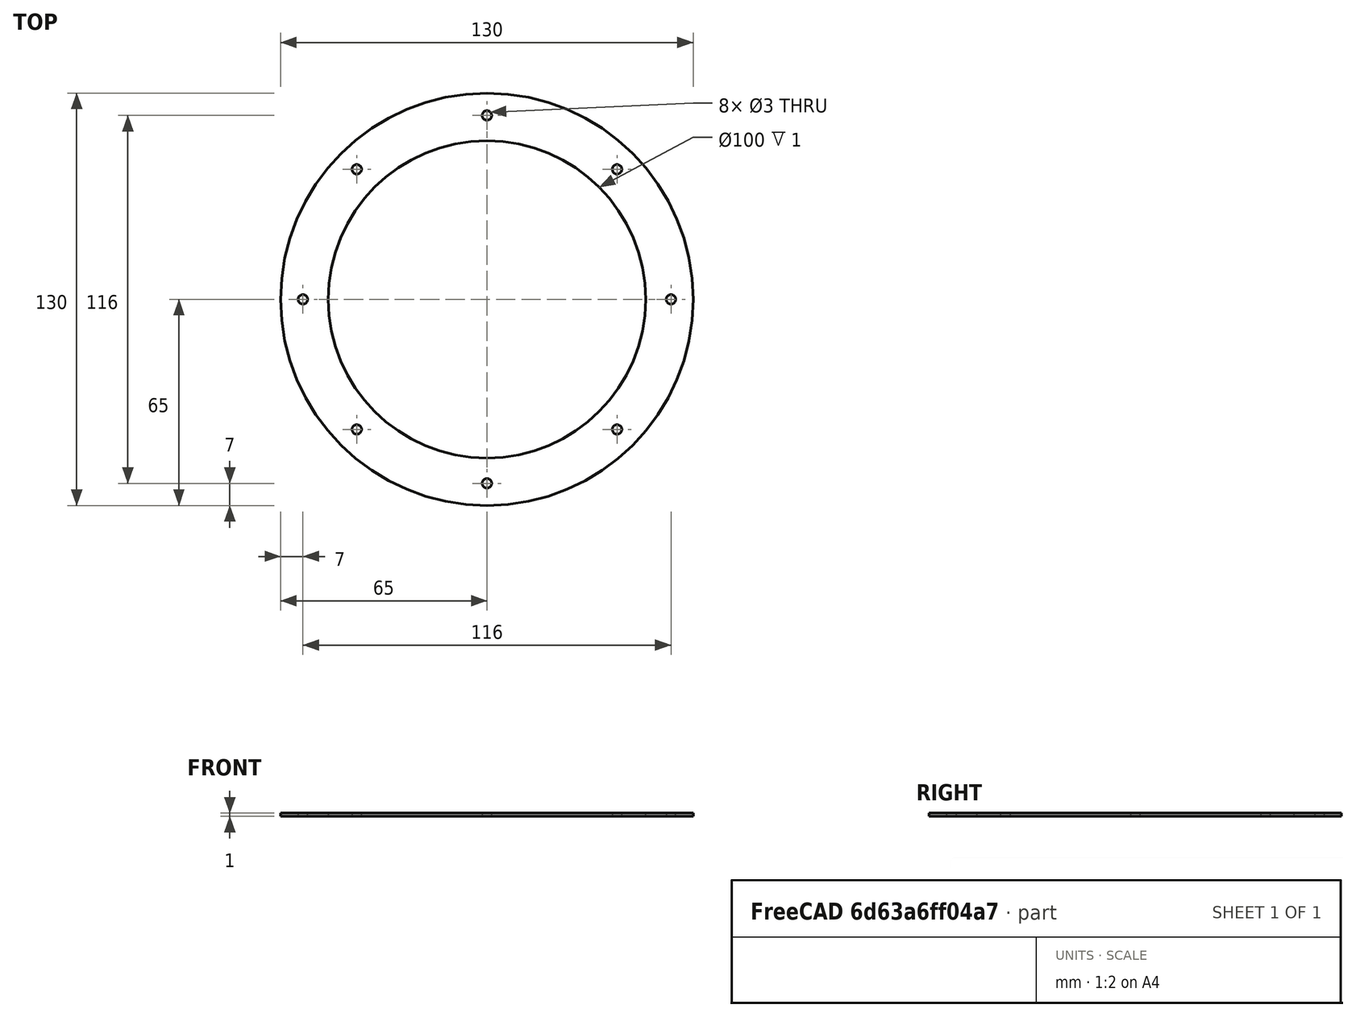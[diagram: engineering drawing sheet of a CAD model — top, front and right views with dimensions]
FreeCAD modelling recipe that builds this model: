
FCSTD DOCUMENT  (FreeCAD 0.18.4R)
Label: Rubber_Ring_II_LightDome
License: CreativeCommons Attribution-ShareAlike
LicenseURL: http://creativecommons.org/licenses/by-sa/4.0/
objects: TechDraw::DrawViewDimension×4, Sketcher::SketchObject×1, Part::Extrusion×1, TechDraw::DrawSVGTemplate×1, TechDraw::DrawViewPart×1, TechDraw::DrawViewAnnotation×1, TechDraw::DrawGeomHatch×1, TechDraw::DrawPage×1
note: 2 computed .brp shape members not serialized (recipe doc carries the construction recipe); baked Part::Feature solids carry a one-line shape summary decoded from their .brp

FEATURE [Sketcher::SketchObject] Sketch
  sketch-geometry (18):
    g0: Circle CenterX=0 CenterY=0 CenterZ=0 NormalX=0 NormalY=0 NormalZ=1 AngleXU=0 Radius=65
    g1: LineSegment [constr] StartX=-70 StartY=70 StartZ=0 EndX=70 EndY=70 EndZ=0
    g2: LineSegment [constr] StartX=70 StartY=70 StartZ=0 EndX=70 EndY=-70 EndZ=0
    g3: LineSegment [constr] StartX=70 StartY=-70 StartZ=0 EndX=-70 EndY=-70 EndZ=0
    g4: LineSegment [constr] StartX=-70 StartY=-70 StartZ=0 EndX=-70 EndY=70 EndZ=0
    g5: LineSegment [constr] StartX=-70 StartY=70 StartZ=0 EndX=70 EndY=-70 EndZ=0
    g6: LineSegment [constr] StartX=70 StartY=70 StartZ=0 EndX=-70 EndY=-70 EndZ=0
    g7: GeomPoint X=0 Y=0 Z=0
    g8: Circle [constr] CenterX=0 CenterY=0 CenterZ=0 NormalX=0 NormalY=0 NormalZ=1 AngleXU=0 Radius=58
    g9: Circle CenterX=0 CenterY=0 CenterZ=0 NormalX=0 NormalY=0 NormalZ=1 AngleXU=0 Radius=50
    g10: Circle CenterX=-41.0122 CenterY=41.0122 CenterZ=0 NormalX=0 NormalY=0 NormalZ=1 AngleXU=0 Radius=1.5
    g11: Circle CenterX=0 CenterY=58 CenterZ=0 NormalX=0 NormalY=0 NormalZ=1 AngleXU=0 Radius=1.5
    g12: Circle CenterX=58 CenterY=0 CenterZ=0 NormalX=0 NormalY=0 NormalZ=1 AngleXU=0 Radius=1.5
    g13: Circle CenterX=0 CenterY=-58 CenterZ=0 NormalX=0 NormalY=0 NormalZ=1 AngleXU=0 Radius=1.5
    g14: Circle CenterX=-41.0122 CenterY=-41.0122 CenterZ=0 NormalX=0 NormalY=0 NormalZ=1 AngleXU=0 Radius=1.5
    g15: Circle CenterX=-58 CenterY=0 CenterZ=0 NormalX=0 NormalY=0 NormalZ=1 AngleXU=0 Radius=1.5
    g16: Circle CenterX=41.0122 CenterY=-41.0122 CenterZ=0 NormalX=0 NormalY=0 NormalZ=1 AngleXU=0 Radius=1.5
    g17: Circle CenterX=41.0122 CenterY=41.0122 CenterZ=0 NormalX=0 NormalY=0 NormalZ=1 AngleXU=0 Radius=1.5
  constraints (49):
    c: Coincident(g0,g-1)
    c: Radius(g0) = 65
    c: Coincident(g1,g2)
    c: Coincident(g2,g3)
    c: Coincident(g3,g4)
    c: Coincident(g4,g1)
    c: Horizontal(g1)
    c: Horizontal(g3)
    c: Vertical(g2)
    c: Vertical(g4)
    c: PointOnObject(g7,g5)
    c: PointOnObject(g7,g6)
    c: Coincident(g6,g1)
    c: Coincident(g5,g1)
    c: Coincident(g6,g3)
    c: Coincident(g5,g2)
    c: Coincident(g7,g0)
    c: Equal(g1,g4)
    c: Equal(g4,g2)
    c: Equal(g2,g3)
    c: DistanceX(g1,g1) = 140
    c: Radius(g8) = 58
    c: Coincident(g8,g0)
    c: Radius(g9) = 50
    c: Coincident(g9,g0)
    c: Radius(g10) = 1.5
    c: PointOnObject(g10,g8)
    c: PointOnObject(g10,g5)
    c: Radius(g11) = 1.5
    c: PointOnObject(g11,g-2)
    c: PointOnObject(g11,g8)
    c: Radius(g17) = 1.5
    c: PointOnObject(g17,g6)
    c: PointOnObject(g17,g8)
    c: Radius(g12) = 1.5
    c: PointOnObject(g12,g-1)
    c: PointOnObject(g12,g8)
    c: Radius(g16) = 1.5
    c: PointOnObject(g16,g5)
    c: PointOnObject(g16,g8)
    c: Radius(g13) = 1.5
    c: PointOnObject(g13,g-2)
    c: PointOnObject(g13,g8)
    c: Radius(g14) = 1.5
    c: PointOnObject(g14,g6)
    c: PointOnObject(g14,g8)
    c: Radius(g15) = 1.5
    c: PointOnObject(g15,g-1)
    c: PointOnObject(g15,g8)
FEATURE [Part::Extrusion] Extrude
  Base = -> Sketch
  Dir = (0,0,1)
  DirMode = 2
  FaceMakerClass = Part::FaceMakerBullseye
  LengthFwd = 1
  LengthRev = 0
  Solid = true
  Symmetric = false
FEATURE [TechDraw::DrawSVGTemplate] Template
  EditableTexts = AUTHOR_NAME=Norman Rembarz; DN=1; DRAWING_TITLE=REGREEN - SensoLAB; FC-DATE=30/10/2020; FC-REV=REV A; FC-SC=1:1; FC-SH=1; FC-SI=A4; FreeCAD_DRAWING=for light-dome module; PN=LAB-LD-Ri01; SI-1=rubber ring No.01; SI-3=REGREEN PROJECT of EU
  Height = 210
  Orientation = 1
  Width = 297
FEATURE [TechDraw::DrawViewPart] View  label="Draufsicht"
  CoarseView = false
  Direction = (0,0,1)
  Focus = 100
  HardHidden = false
  IsoCount = 0
  IsoHidden = false
  IsoVisible = false
  LockPosition = false
  Perspective = false
  Rotation = 0
  ScaleType = 0
  SeamHidden = false
  SeamVisible = false
  SmoothHidden = false
  SmoothVisible = false
  Source = -> [Extrude]
  X = 90.9429
  Y = 121.373
FEATURE [TechDraw::DrawViewDimension] Dimension
  Arbitrary = false
  FormatSpec = ⌀%.2f
  LockPosition = false
  MeasureType = 1
  OverTolerance = 0
  References2D = -> [View]
  Rotation = 0
  ScaleType = 0
  Type = 5
  UnderTolerance = 0
  X = 54.0601
  Y = 60.3725
FEATURE [TechDraw::DrawViewDimension] Dimension001
  Arbitrary = false
  FormatSpec = ⌀%.2f
  LockPosition = false
  MeasureType = 1
  OverTolerance = 0
  References2D = -> [View]
  Rotation = 0
  ScaleType = 0
  Type = 5
  UnderTolerance = 0
  X = 76.72
  Y = 49.8518
FEATURE [TechDraw::DrawViewDimension] Dimension002
  Arbitrary = false
  FormatSpec = ⌀%.2f
  LockPosition = false
  MeasureType = 1
  OverTolerance = 0
  References2D = -> [View]
  Rotation = 0
  ScaleType = 0
  Type = 5
  UnderTolerance = 0
  X = 82.2771
  Y = 8.20523
FEATURE [TechDraw::DrawViewAnnotation] Annotation
  Font = osifont
  LineSpace = 80
  LockPosition = false
  MaxWidth = -1
  Rotation = 0
  ScaleType = 0
  Text = thickness of rubber material | should be 1mm
  TextSize = 5
  TextStyle = 0
  X = 217.723
  Y = 63.9791
FEATURE [TechDraw::DrawGeomHatch] GeomHatch  label="GeomHatchFX0"
  FilePattern = /Applications/FreeCAD.app/Contents/Resources/data/Mod/TechDraw/PAT/FCPAT.pat
  NamePattern = Diagonal4
  ScalePattern = 1
  Source = -> View [Face0]
FEATURE [TechDraw::DrawViewDimension] Dimension003
  Arbitrary = false
  FormatSpec = %.2f
  LockPosition = false
  MeasureType = 1
  OverTolerance = 0
  References2D = -> [View]
  Rotation = 0
  ScaleType = 0
  Type = 2
  UnderTolerance = 0
  X = 0.233073
  Y = -24.1055
FEATURE [TechDraw::DrawPage] Page
  KeepUpdated = true
  ProjectionType = 0
  Template = -> Template
  Views = -> [View,Dimension,Dimension001,Dimension002,Annotation,Dimension003]
